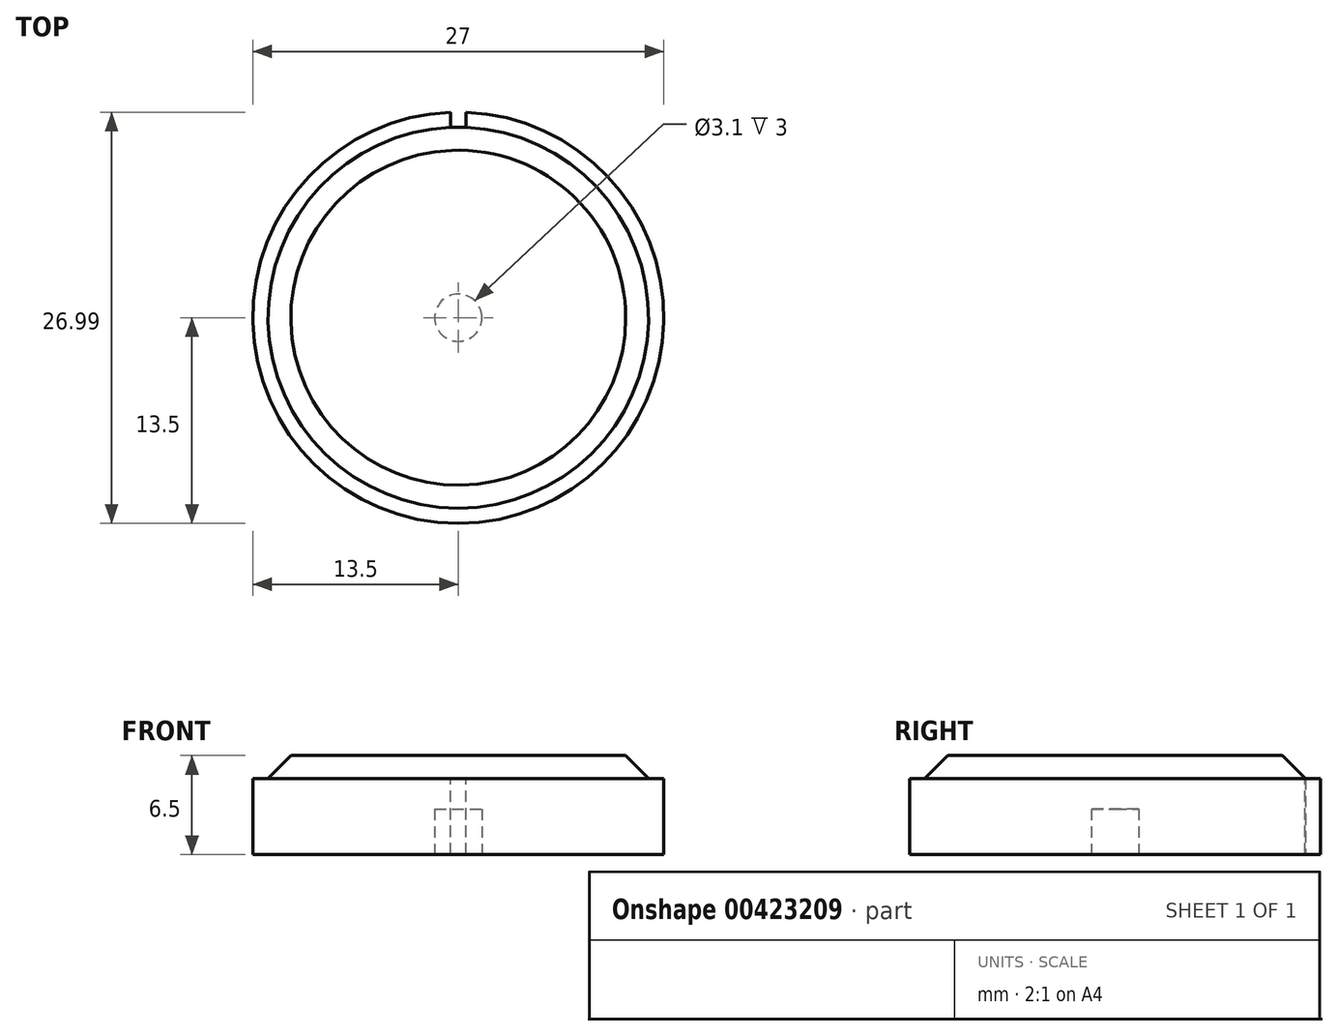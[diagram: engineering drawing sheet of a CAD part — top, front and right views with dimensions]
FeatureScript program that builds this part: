
annotation { "Feature Type Name" : "Feature", "Feature Type Description" : "" }
export const myFeature = defineFeature(function(context is Context, id is Id, definition is map)
    precondition{}
    {
        {
            var Q0;
            Q0=qCreatedBy(makeId("Top.planeOp"),FACE);
            var sketch = newSketch(context, id + "F0", { "sketchPlane" : qUnion([Q0])});
            skCircle(sketch, "E0", {"center": v(0, 0) * mm, "radius": 13.5 * mm});
            skSolve(sketch);
        }
        {
            var Q0;
            Q0 = qSketchRegion(id + "F0", true);
            extrude(context, id + "F1", {"entities" : qUnion([Q0]), "depth" : 5 * mm});
        }
        {
            var Q0;
            Q0=makeQuery(id+"F1.opExtrude","CAP_FACE",FACE,{"disambiguationData":[OSD([sQuery(id+"F0.wireOp",EDGE,"E0")])],"isStart":false});
            var sketch = newSketch(context, id + "F2", { "sketchPlane" : qUnion([Q0])});
            skCircle(sketch, "E1", {"center": v(0, 0) * mm, "radius": 12.5 * mm});
            skSolve(sketch);
        }
        {
            var Q0;
            Q0 = qSketchRegion(id + "F2", true);
            extrude(context, id + "F3", {"entities" : qUnion([Q0]), "operationType" : NewBodyOperationType.ADD, "depth" : 1.5 * mm});
        }
        {
            var Q0;
            Q0=makeQuery(id+"F1.opExtrude","CAP_FACE",FACE,{"disambiguationData":[OSD([sQuery(id+"F0.wireOp",EDGE,"E0")])],"isStart":false});
            var sketch = newSketch(context, id + "F4", { "sketchPlane" : qUnion([Q0])});
            skLineSegment(sketch, "E2.bottom", {"start": v(-0.5, 14.66) * mm, "end": v(0.5, 14.66) * mm});
            skLineSegment(sketch, "E2.top", {"start": v(-0.5, 10.34) * mm, "end": v(0.5, 10.34) * mm});
            skLineSegment(sketch, "E2.left", {"start": v(-0.5, 14.66) * mm, "end": v(-0.5, 10.34) * mm});
            skLineSegment(sketch, "E2.right", {"start": v(0.5, 14.66) * mm, "end": v(0.5, 10.34) * mm});
            skPoint(sketch, "E2.middle", {"position": v(0, 12.5) * mm});
            skSolve(sketch);
        }
        {
            var Q0;
            {var subQ0=sQuery(id+"F4.wireOp",EDGE,"E2.left");var subQ1=makeQuery(id+"F1.opExtrude","CAP_EDGE",EDGE,{"disambiguationData":[OSD([sQuery(id+"F0.wireOp",EDGE,"E0")])],"isStart":false});var subQ2=makeQuery(id+"F4.imprint","INTERSECT",VERTEX,{"derivedFrom":[subQ1,subQ0]});Q0=makeQuery(id+"F4.imprint","IMPRINT",FACE,{"disambiguationData":[TD([[makeQuery(id+"F4.imprint","IMPRINT",EDGE,{"disambiguationData":[TD([[subQ2,-1.0]])],"derivedFrom":subQ0}),1.0]])]});}
            extrude(context, id + "F5", {"entities" : qUnion([Q0]), "operationType" : NewBodyOperationType.REMOVE, "oppositeDirection" : true, "depth" : 25 * mm});
        }
        {
            var Q0;
            Q0=makeQuery(id+"F3.opExtrude","CAP_EDGE",EDGE,{"disambiguationData":[OSD([sQuery(id+"F2.wireOp",EDGE,"E1")])],"isStart":false});
            chamfer(context, id + "F6", {"entities" : qUnion([Q0]), "width" : 1.5 * mm, "tangentPropagation" : true});
        }
        {
            var Q0;
            Q0=makeQuery(id+"F1.opExtrude","CAP_FACE",FACE,{"disambiguationData":[OSD([sQuery(id+"F0.wireOp",EDGE,"E0")])],"isStart":true});
            var sketch = newSketch(context, id + "F7", { "sketchPlane" : qUnion([Q0])});
            skCircle(sketch, "E3", {"center": v(0, 0) * mm, "radius": 1.55 * mm});
            skSolve(sketch);
        }
        {
            var Q0;
            Q0=makeQuery(id+"F7.imprint","IMPRINT",FACE,{"disambiguationData":[TD([[makeQuery(id+"F7.imprint","IMPRINT",EDGE,{"derivedFrom":sQuery(id+"F7.wireOp",EDGE,"E3")}),1.0]])]});
            extrude(context, id + "F8", {"entities" : qUnion([Q0]), "operationType" : NewBodyOperationType.REMOVE, "oppositeDirection" : true, "depth" : 3 * mm});
        }
    });
